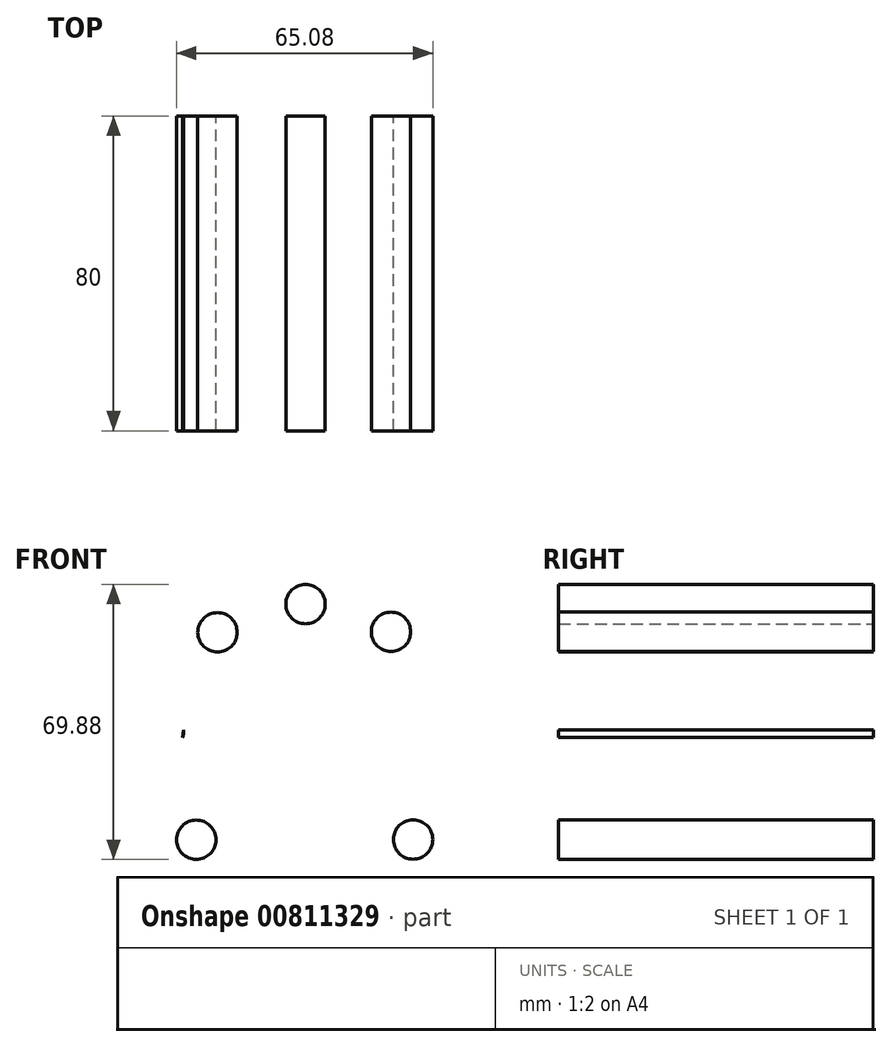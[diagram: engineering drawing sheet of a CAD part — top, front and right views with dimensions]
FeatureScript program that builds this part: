
annotation { "Feature Type Name" : "Feature", "Feature Type Description" : "" }
export const myFeature = defineFeature(function(context is Context, id is Id, definition is map)
    precondition{}
    {
        {
            var Q0;
            Q0=qCreatedBy(makeId("Front.planeOp"),FACE);
            var sketch = newSketch(context, id + "F0", { "sketchPlane" : qUnion([Q0])});
            skCircle(sketch, "E0", {"center": v(-1.6, 0) * mm, "radius": 31 * mm});
            skCircle(sketch, "E1", {"center": v(-23.66, 29.05) * mm, "radius": 5 * mm});
            skCircle(sketch, "E2.1.0", {"center": v(-37.27, 3.81) * mm, "radius": 5 * mm});
            skCircle(sketch, "E2.2.0", {"center": v(-29.05, -23.66) * mm, "radius": 5 * mm});
            skPoint(sketch, "E2.center", {"position": v(0, 0) * mm});
            skCircle(sketch, "E3", {"center": v(0.3, -35.77) * mm, "radius": 5 * mm});
            skCircle(sketch, "E4", {"center": v(20.41, 29.18) * mm, "radius": 5 * mm});
            skCircle(sketch, "E5", {"center": v(26.03, -23.6) * mm, "radius": 5 * mm});
            skCircle(sketch, "E6", {"center": v(-1.3, 36.22) * mm, "radius": 5 * mm});
            skSolve(sketch);
        }
        {
            var Q0;
            {var subQ0=sQuery(id+"F0.wireOp",EDGE,"E2.1.0");var subQ1=sQuery(id+"F0.wireOp",EDGE,"E0");var subQ2=makeQuery(id+"F0.imprint","INTERSECT",VERTEX,{"disambiguationData":[OD(0.0)],"derivedFrom":[subQ1,subQ0]});Q0=makeQuery(id+"F0.imprint","IMPRINT",FACE,{"disambiguationData":[TD([[makeQuery(id+"F0.imprint","IMPRINT",EDGE,{"disambiguationData":[TD([[subQ2,-1.0]])],"derivedFrom":subQ1}),1.0]])]});}
            var Q1;
            Q1=makeQuery(id+"F0.imprint","IMPRINT",FACE,{"disambiguationData":[TD([[makeQuery(id+"F0.imprint","IMPRINT",EDGE,{"derivedFrom":sQuery(id+"F0.wireOp",EDGE,"E4")}),1.0]])]});
            var Q2;
            Q2=makeQuery(id+"F0.imprint","IMPRINT",FACE,{"disambiguationData":[TD([[makeQuery(id+"F0.imprint","IMPRINT",EDGE,{"derivedFrom":sQuery(id+"F0.wireOp",EDGE,"E6")}),1.0]])]});
            var Q3;
            Q3=makeQuery(id+"F0.imprint","IMPRINT",FACE,{"disambiguationData":[TD([[makeQuery(id+"F0.imprint","IMPRINT",EDGE,{"derivedFrom":sQuery(id+"F0.wireOp",EDGE,"E1")}),1.0]])]});
            var Q4;
            {var subQ0=sQuery(id+"F0.wireOp",EDGE,"E2.1.0");var subQ1=sQuery(id+"F0.wireOp",EDGE,"E0");var subQ2=makeQuery(id+"F0.imprint","INTERSECT",VERTEX,{"disambiguationData":[OD(0.0)],"derivedFrom":[subQ1,subQ0]});Q4=makeQuery(id+"F0.imprint","IMPRINT",FACE,{"disambiguationData":[TD([[makeQuery(id+"F0.imprint","IMPRINT",EDGE,{"disambiguationData":[TD([[subQ2,1.0]])],"derivedFrom":subQ1}),-1.0]])]});}
            var Q5;
            Q5=makeQuery(id+"F0.imprint","IMPRINT",FACE,{"disambiguationData":[TD([[makeQuery(id+"F0.imprint","IMPRINT",EDGE,{"derivedFrom":sQuery(id+"F0.wireOp",EDGE,"E2.2.0")}),1.0]])]});
            var Q6;
            {var subQ0=sQuery(id+"F0.wireOp",EDGE,"E3");var subQ1=sQuery(id+"F0.wireOp",EDGE,"E0");var subQ2=makeQuery(id+"F0.imprint","INTERSECT",VERTEX,{"disambiguationData":[OD(0.0)],"derivedFrom":[subQ1,subQ0]});Q6=makeQuery(id+"F0.imprint","IMPRINT",FACE,{"disambiguationData":[TD([[makeQuery(id+"F0.imprint","IMPRINT",EDGE,{"disambiguationData":[TD([[subQ2,-1.0]])],"derivedFrom":subQ1}),-1.0]])]});}
            var Q7;
            Q7=makeQuery(id+"F0.imprint","IMPRINT",FACE,{"disambiguationData":[TD([[makeQuery(id+"F0.imprint","IMPRINT",EDGE,{"derivedFrom":sQuery(id+"F0.wireOp",EDGE,"E5")}),1.0]])]});
            extrude(context, id + "F1", {"entities" : qUnion([Q0, Q1, Q2, Q3, Q4, Q5, Q6, Q7]), "depth" : 80 * mm, "offsetDistance" : 25 * mm});
        }
    });
